# Revit family: 210_e043900bc1dc4065a8cf497bf579gb
name_source: partatom
category: Mechanical Equipment
units: mm (PartAtom-declared; Revit-internal decimal feet)

## family parameters
Always vertical = Yes
Classification = None
Cut with Voids When Loaded = No
Part Type = Normal
Room Calculation Point = No
Round Connector Dimension = Use Diameter
Shared = No
Work Plane-Based = No

## types (1)
- Vallox 51 MV R, no heater
    BBVIS = No
    BH = 725 mm  [stored 2.37861 ft]
    BW = 359 mm  [stored 1.17782 ft]
    CAT = No
    CenSd_DPR_8 = 7 mm  [stored 0.0229659 ft]
    CenSd_EPR_6 = 26 mm  [stored 0.0853018 ft]
    D = 125 mm
    DEC = 81 mm  [stored 0.265748 ft]
    DEX = 377 mm  [stored 1.23688 ft]
    DEXY = 145 mm  [stored 0.475722 ft]
    DL = 15 mm  [stored 0.0492126 ft]
    DOC = 518 mm  [stored 1.69948 ft]
    DPR = 8 mm  [stored 0.0262467 ft]
    DR = 23 mm
    DR1 = 18 mm
    DR2 = 6 mm  [stored 0.019685 ft]
    DR3 = 10 mm  [stored 0.0328084 ft]
    DR4 = 12 mm
    DSC = 222 mm  [stored 0.728346 ft]
    DSCY = 105 mm  [stored 0.344488 ft]
    D_2 = 63 mm
    Default Elevation = 0 mm  [stored 0 ft]
    Description = Ventilation unit
    E = 110 mm  [stored 0.360892 ft]
    ENBL350 = No
    EPR = 30 mm  [stored 0.0984252 ft]
    ER = 26 mm  [stored 0.0853018 ft]
    ER1 = 20 mm  [stored 0.0656168 ft]
    H = 668 mm  [stored 2.1916 ft]
    H2 = 668 mm  [stored 2.1916 ft]
    HB = 648 mm  [stored 2.12598 ft]
    HP = 339 mm  [stored 1.1122 ft]
    HP1 = 658 mm  [stored 2.15879 ft]
    HZ = 673 mm  [stored 2.20801 ft]
    L = 598 mm  [stored 1.96194 ft]
    LD = 89 mm  [stored 0.291995 ft]
    LLDAndHLD = Yes
    LLDONLY = Yes
    LP1 = 588 mm  [stored 1.92913 ft]
    L_2 = 299 mm  [stored 0.980971 ft]
    MC Active Power = 940 W
    MC Apparent Power = 940 VA
    MC CosPhi = 1
    MC Enable LOD 200 = No
    MC Enable LOD 350 = No
    MC Material1 MAIN_MODEL = MC_255_255_255_0_50
    MC Material12 MAIN_MODEL = MC_128_128_128_0_50
    MC Material13 MAIN_MODEL = MC_255_255_255_60_50
    MC Material14 MAIN_MODEL = MC_191_191_191_0_50
    MC Material4 MAIN_MODEL = MC_0_0_0_0_50
    MC Number of Poles = 1
    MC Product Code = Vallox 51 MV R, no heater
    MC Voltage = 230 V
    MP = No
    MPH = 46 mm  [stored 0.150919 ft]
    MPH1 = 44 mm  [stored 0.144357 ft]
    MPS = 2 mm  [stored 0.00656168 ft]
    MP_LLDAndHLD = No
    Manufacturer = Vallox
    QmdConnectorList = 221;D;231;D;241;D;251;D
    RS = 63 mm
    S = 1 mm  [stored 0.00328084 ft]
    SE = 0 mm  [stored 0 ft]
    URL = www.vallox.com
    VIS0 = No
    W = 339 mm  [stored 1.1122 ft]
    W_2 = 170 mm  [stored 0.557743 ft]
    magiPartTypeId = 210
    magiProductFamilyId = e043900bc1dc4065a8cf497bf579gb
    magiProductId = e043900bc1dc4065a8cf497bf579gb

note: [stored X ft] marks values corroborated as IEEE doubles in the binary element streams (Revit-internal decimal feet)

## geometry (parser evidence)
native form markers: Sweep x2
no freeform markers — native parametric forms only
